# Revit family: Temper_83_КранШаровый-ВВ_Бабочка_GAS
name_source: partatom
category: Арматура трубопроводов
units: mm (PartAtom-declared; Revit-internal decimal feet)

## family parameters
Всегда вертикально = Да
На основе рабочей плоскости = Нет
Общий = Нет
При загрузке вырезать с полостями = Нет
Размер круглого соединителя = Использовать диаметр
Тип детали = Вставляется

## types (4) — shared parameters
ADSK_URL документации изделия = https://brass.temper.ru
ADSK_URL страницы изделия = https://brass.temper.ru
ADSK_Версия Revit = 2019
ADSK_Версия семейства = v1.0
ADSK_Единица измерения = шт.
ADSK_Завод-изготовитель = ООО «ТД «Темпер»
ADSK_Количество = 1
ADSK_Материал = Латунь ЛС59-1В
ADSK_Наименование краткое = Кран шаровой латунный Temper
ADSK_Обозначение = ГОСТ Р 59553-2021
N = 1
Изготовитель = ООО «ТД «Темпер»
Разработчик = https://3dbim.pro
ТВ = ВВ
ТВ1 = temper

## per-type parameters (varying)
| type | ADSK_Диаметр условный | ADSK_Код изделия | ADSK_Марка | ADSK_Масса | ADSK_Масса_Текст | ADSK_Наименование |
| DN 15 | 15 мм | 8315ВВБ1240 | 8315ВВБ1240 | 0.146 | 0.146 | Кран шаровый латунный Temper для газа DN15 (12”) PN40 внутренняявнутренняя бабочка GAS |
| DN 20 | 20 мм | 8320ВВБ3440 | 8320ВВБ3440 | 0.201 | 0.201 | Кран шаровый латунный Temper для газа DN20 (34”) PN40 внутренняявнутренняя бабочка GAS |
| DN 32 | 32 мм | 8332ВВБ11425 | 8332ВВБ11425 | 0.555 | 0.555 | Кран шаровый латунный Temper для газа DN32 (1 14”) PN25 внутренняявнутренняя бабочка GAS |
| DN 25 | 25 мм | 8325ВВБ140 | 8325ВВБ140 | 0.311 | 0.311 | Кран шаровый латунный Temper для газа  DN25 (1”) PN40 внутренняявнутренняя бабочка GAS |
